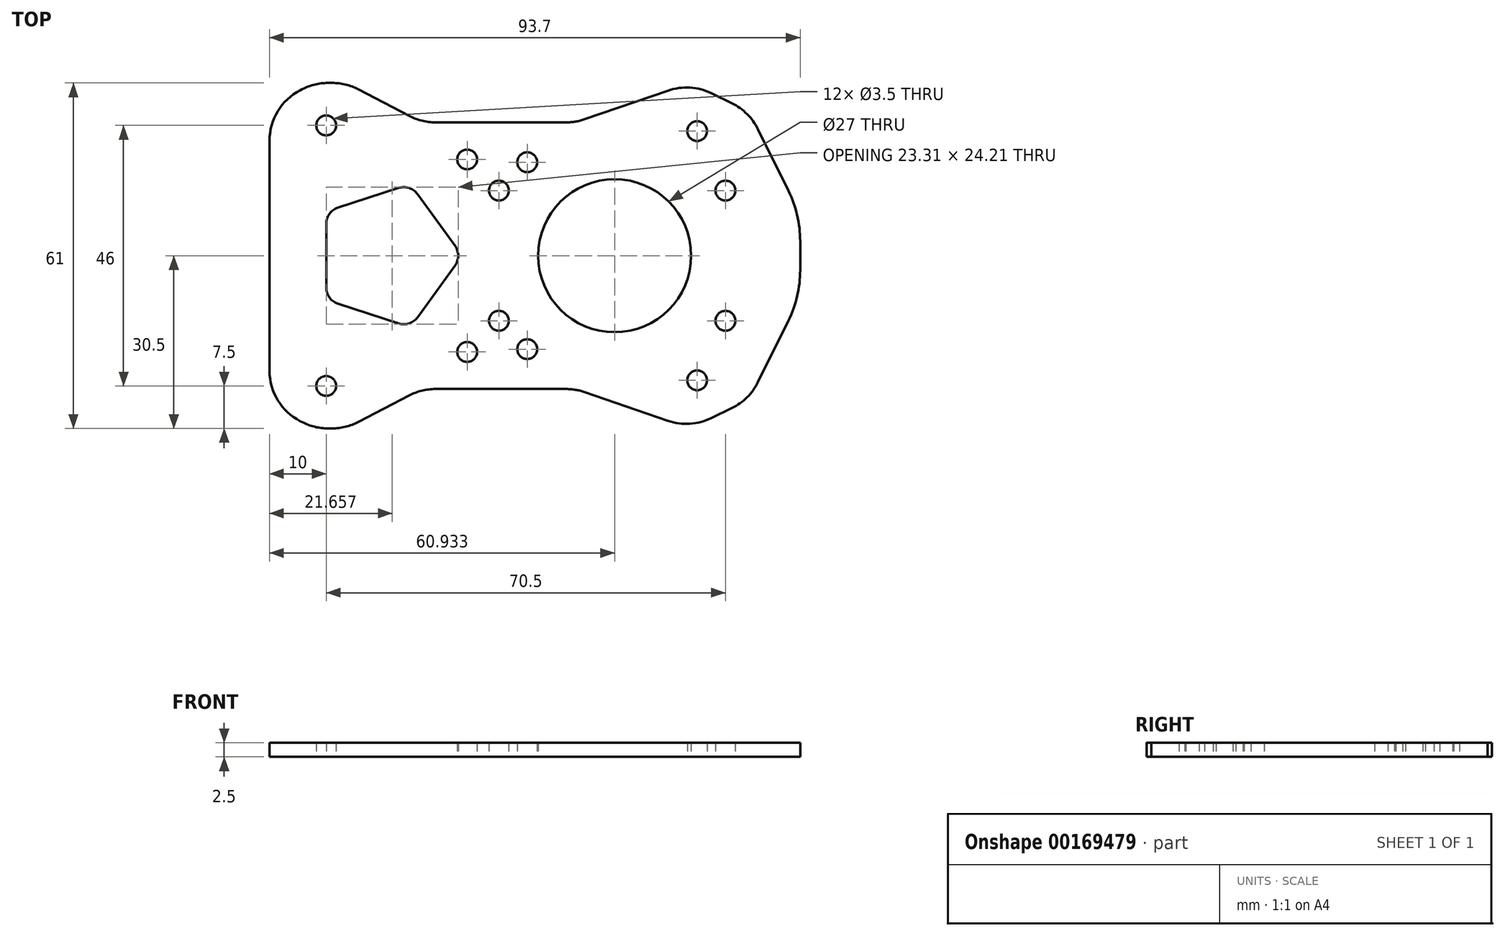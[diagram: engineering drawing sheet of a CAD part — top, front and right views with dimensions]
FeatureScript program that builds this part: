
annotation { "Feature Type Name" : "Feature", "Feature Type Description" : "" }
export const myFeature = defineFeature(function(context is Context, id is Id, definition is map)
    precondition{}
    {
        {
            var Q0;
            Q0=qCreatedBy(makeId("Top.planeOp"),FACE);
            var sketch = newSketch(context, id + "F0", { "sketchPlane" : qUnion([Q0])});
            skLineSegment(sketch, "E0.bottom", {"start": v(0, 0) * mm, "end": v(20, 0) * mm});
            skLineSegment(sketch, "E0.top", {"start": v(0, 80) * mm, "end": v(20, 80) * mm});
            skLineSegment(sketch, "E0.left", {"start": v(0, 0) * mm, "end": v(0, 80) * mm});
            skLineSegment(sketch, "E0.right", {"start": v(20, 0) * mm, "end": v(20, 11.5) * mm});
            skLineSegment(sketch, "E1.bottom", {"start": v(20, 11.5) * mm, "end": v(50, 11.5) * mm});
            skLineSegment(sketch, "E1.top", {"start": v(20, 68.5) * mm, "end": v(50, 68.5) * mm});
            skLineSegment(sketch, "E1.right", {"start": v(50, 11.5) * mm, "end": v(50, 68.5) * mm});
            skPoint(sketch, "E2", {"position": v(20, 40) * mm});
            skLineSegment(sketch, "E3.trimOffspring", {"start": v(20, 68.5) * mm, "end": v(20, 80) * mm});
            skLineSegment(sketch, "E4", {"start": v(10, 0) * mm, "end": v(0, 10) * mm});
            skLineSegment(sketch, "E5", {"start": v(0, 70) * mm, "end": v(10, 80) * mm});
            skLineSegment(sketch, "E6", {"start": v(0, 40) * mm, "end": v(50, 40) * mm, "construction": true});
            skLineSegment(sketch, "E7", {"start": v(0, 57) * mm, "end": v(50, 57) * mm, "construction": true});
            skLineSegment(sketch, "E8", {"start": v(0, 23) * mm, "end": v(50, 23) * mm, "construction": true});
            skLineSegment(sketch, "E9", {"start": v(14.5, 80) * mm, "end": v(14.5, 0) * mm, "construction": true});
            skCircle(sketch, "E10", {"center": v(14.5, 69.5) * mm, "radius": 2 * mm});
            skCircle(sketch, "E11", {"center": v(14.5, 75.5) * mm, "radius": 1.5 * mm});
            skCircle(sketch, "E12", {"center": v(14.5, 63) * mm, "radius": 1.75 * mm});
            skCircle(sketch, "E13.MirrorC", {"center": v(14.5, 17) * mm, "radius": 1.75 * mm});
            skCircle(sketch, "E14.MirrorC", {"center": v(14.5, 4.5) * mm, "radius": 1.5 * mm});
            skCircle(sketch, "E15.MirrorC", {"center": v(14.5, 10.5) * mm, "radius": 2 * mm});
            skLineSegment(sketch, "E16.0", {"start": v(0, 20.5) * mm, "end": v(50, 20.5) * mm});
            skLineSegment(sketch, "E17.0", {"start": v(0, 25.5) * mm, "end": v(50, 25.5) * mm});
            skLineSegment(sketch, "E18.MirrorCS", {"start": v(0, 54.5) * mm, "end": v(50, 54.5) * mm});
            skLineSegment(sketch, "E19.MirrorCS", {"start": v(0, 59.5) * mm, "end": v(50, 59.5) * mm});
            skSolve(sketch);
        }
        {
            var Q0;
            Q0=qCreatedBy(makeId("Top.planeOp"),FACE);
            var sketch = newSketch(context, id + "F1", { "sketchPlane" : qUnion([Q0])});
            skLineSegment(sketch, "E20", {"start": v(4.5, 70.5) * mm, "end": v(18, 70.5) * mm, "construction": true});
            skLineSegment(sketch, "E21", {"start": v(18, 70.5) * mm, "end": v(26.93, 67) * mm, "construction": true});
            skLineSegment(sketch, "E22", {"start": v(26.93, 67) * mm, "end": v(95, 67) * mm, "construction": true});
            skLineSegment(sketch, "E23", {"start": v(95, 67) * mm, "end": v(95, 40) * mm, "construction": true});
            skLineSegment(sketch, "E24", {"start": v(95, 40) * mm, "end": v(4.5, 40) * mm, "construction": true});
            skLineSegment(sketch, "E25", {"start": v(4.5, 40) * mm, "end": v(4.5, 70.5) * mm, "construction": true});
            skLineSegment(sketch, "E26.MirrorCS", {"start": v(95, 13) * mm, "end": v(95, 40) * mm, "construction": true});
            skLineSegment(sketch, "E27.MirrorCS", {"start": v(26.93, 13) * mm, "end": v(95, 13) * mm, "construction": true});
            skLineSegment(sketch, "E28.MirrorCS", {"start": v(18, 9.5) * mm, "end": v(26.93, 13) * mm, "construction": true});
            skLineSegment(sketch, "E29.MirrorCS", {"start": v(4.5, 9.5) * mm, "end": v(18, 9.5) * mm, "construction": true});
            skLineSegment(sketch, "E30.MirrorCS", {"start": v(4.5, 40) * mm, "end": v(4.5, 9.5) * mm, "construction": true});
            skCircle(sketch, "E31", {"center": v(80, 62) * mm, "radius": 1.75 * mm});
            skCircle(sketch, "E32", {"center": v(80, 18) * mm, "radius": 1.75 * mm});
            skCircle(sketch, "E33", {"center": v(85, 51.5) * mm, "radius": 1.75 * mm});
            skCircle(sketch, "E34", {"center": v(85, 28.5) * mm, "radius": 1.75 * mm});
            skLineSegment(sketch, "E35", {"start": v(32.12, 40) * mm, "end": v(170.35, 40) * mm, "construction": true});
            skCircle(sketch, "E36", {"center": v(50, 23.5) * mm, "radius": 1.75 * mm});
            skCircle(sketch, "E37", {"center": v(50, 56.5) * mm, "radius": 1.75 * mm});
            skCircle(sketch, "E38", {"center": v(45, 51.5) * mm, "radius": 1.75 * mm});
            skCircle(sketch, "E39", {"center": v(45, 28.5) * mm, "radius": 1.75 * mm});
            skCircle(sketch, "E40", {"center": v(65.43, 40) * mm, "radius": 13.5 * mm});
            skCircle(sketch, "E41.0", {"center": v(14.5, 63) * mm, "radius": 1.75 * mm});
            skCircle(sketch, "E42.0", {"center": v(14.5, 17) * mm, "radius": 1.75 * mm});
            skCircle(sketch, "E43", {"center": v(39.4, 57) * mm, "radius": 1.75 * mm});
            skCircle(sketch, "E44.MirrorC", {"center": v(39.4, 23) * mm, "radius": 1.75 * mm});
            skLineSegment(sketch, "E45", {"start": v(9.9, 69.2) * mm, "end": v(10.24, 69.38) * mm});
            skLineSegment(sketch, "E46", {"start": v(14.84, 70.5) * mm, "end": v(15.55, 70.5) * mm});
            skLineSegment(sketch, "E47", {"start": v(20.18, 69.37) * mm, "end": v(29.16, 64.68) * mm});
            skLineSegment(sketch, "E48", {"start": v(33.8, 63.54) * mm, "end": v(56.89, 63.54) * mm});
            skLineSegment(sketch, "E49", {"start": v(60.14, 64.09) * mm, "end": v(74.87, 69.15) * mm});
            skLineSegment(sketch, "E50", {"start": v(82.52, 68.68) * mm, "end": v(86.17, 66.9) * mm});
            skLineSegment(sketch, "E51", {"start": v(90.74, 62.34) * mm, "end": v(96.12, 51.45) * mm});
            skLineSegment(sketch, "E52", {"start": v(98.2, 42.58) * mm, "end": v(98.2, 40) * mm});
            skLineSegment(sketch, "E53", {"start": v(4.5, 60.32) * mm, "end": v(4.5, 40) * mm});
            skPoint(sketch, "E54.visualSharp", {"position": v(4.5, 66.4) * mm});
            skArc(sketch, "E54.filletArc", {"start": v(9.9, 69.2) * mm, "mid": v(5.96, 65.52) * mm, "end": v(4.5, 60.32) * mm});
            skPoint(sketch, "E55.visualSharp", {"position": v(12.4, 70.5) * mm});
            skArc(sketch, "E55.filletArc", {"start": v(14.84, 70.5) * mm, "mid": v(12.47, 70.22) * mm, "end": v(10.24, 69.38) * mm});
            skPoint(sketch, "E56.visualSharp", {"position": v(18, 70.5) * mm});
            skArc(sketch, "E56.filletArc", {"start": v(20.18, 69.37) * mm, "mid": v(17.94, 70.21) * mm, "end": v(15.55, 70.5) * mm});
            skPoint(sketch, "E57.visualSharp", {"position": v(31.34, 63.54) * mm});
            skArc(sketch, "E57.filletArc", {"start": v(29.16, 64.68) * mm, "mid": v(31.4, 63.83) * mm, "end": v(33.8, 63.54) * mm});
            skPoint(sketch, "E58.visualSharp", {"position": v(58.56, 63.54) * mm});
            skArc(sketch, "E58.filletArc", {"start": v(56.89, 63.54) * mm, "mid": v(58.53, 63.68) * mm, "end": v(60.14, 64.09) * mm});
            skPoint(sketch, "E59.visualSharp", {"position": v(78.8, 70.5) * mm});
            skArc(sketch, "E59.filletArc", {"start": v(82.52, 68.68) * mm, "mid": v(78.74, 69.68) * mm, "end": v(74.87, 69.15) * mm});
            skPoint(sketch, "E60.visualSharp", {"position": v(89.23, 65.4) * mm});
            skArc(sketch, "E60.filletArc", {"start": v(90.74, 62.34) * mm, "mid": v(88.83, 65) * mm, "end": v(86.17, 66.9) * mm});
            skPoint(sketch, "E61.visualSharp", {"position": v(98.2, 47.26) * mm});
            skArc(sketch, "E61.filletArc", {"start": v(98.2, 42.58) * mm, "mid": v(97.67, 47.14) * mm, "end": v(96.12, 51.45) * mm});
            skLineSegment(sketch, "E62.MirrorCS", {"start": v(4.5, 19.68) * mm, "end": v(4.5, 40) * mm});
            skArc(sketch, "E63.MirrorCS", {"start": v(9.9, 10.8) * mm, "mid": v(5.96, 14.48) * mm, "end": v(4.5, 19.68) * mm});
            skLineSegment(sketch, "E64.MirrorCS", {"start": v(9.9, 10.8) * mm, "end": v(10.24, 10.62) * mm});
            skLineSegment(sketch, "E65.MirrorCS", {"start": v(14.84, 9.5) * mm, "end": v(15.55, 9.5) * mm});
            skArc(sketch, "E66.MirrorCS", {"start": v(14.84, 9.5) * mm, "mid": v(12.47, 9.78) * mm, "end": v(10.24, 10.62) * mm});
            skArc(sketch, "E67.MirrorCS", {"start": v(20.18, 10.63) * mm, "mid": v(17.94, 9.79) * mm, "end": v(15.55, 9.5) * mm});
            skLineSegment(sketch, "E68.MirrorCS", {"start": v(20.18, 10.63) * mm, "end": v(29.16, 15.32) * mm});
            skArc(sketch, "E69.MirrorCS", {"start": v(29.16, 15.32) * mm, "mid": v(31.4, 16.17) * mm, "end": v(33.8, 16.46) * mm});
            skLineSegment(sketch, "E70.MirrorCS", {"start": v(33.8, 16.46) * mm, "end": v(56.89, 16.46) * mm});
            skArc(sketch, "E71.MirrorCS", {"start": v(56.89, 16.46) * mm, "mid": v(58.53, 16.32) * mm, "end": v(60.14, 15.91) * mm});
            skLineSegment(sketch, "E72.MirrorCS", {"start": v(60.14, 15.91) * mm, "end": v(74.87, 10.85) * mm});
            skArc(sketch, "E73.MirrorCS", {"start": v(82.52, 11.32) * mm, "mid": v(78.74, 10.32) * mm, "end": v(74.87, 10.85) * mm});
            skLineSegment(sketch, "E74.MirrorCS", {"start": v(82.52, 11.32) * mm, "end": v(86.17, 13.1) * mm});
            skArc(sketch, "E75.MirrorCS", {"start": v(90.74, 17.66) * mm, "mid": v(88.83, 15) * mm, "end": v(86.17, 13.1) * mm});
            skLineSegment(sketch, "E76.MirrorCS", {"start": v(98.2, 37.42) * mm, "end": v(98.2, 40) * mm});
            skLineSegment(sketch, "E77.MirrorCS", {"start": v(90.74, 17.66) * mm, "end": v(96.12, 28.55) * mm});
            skArc(sketch, "E78.MirrorCS", {"start": v(98.2, 37.42) * mm, "mid": v(97.67, 32.86) * mm, "end": v(96.12, 28.55) * mm});
            skCircle(sketch, "E79.cCircle", {"center": v(25.24, 40) * mm, "radius": 10.74 * mm, "construction": true});
            skLineSegment(sketch, "E79.0", {"start": v(30.63, 50.87) * mm, "end": v(37.24, 41.76) * mm});
            skLineSegment(sketch, "E79.1", {"start": v(37.24, 38.24) * mm, "end": v(30.63, 29.13) * mm});
            skLineSegment(sketch, "E79.2", {"start": v(27.27, 28.04) * mm, "end": v(16.57, 31.52) * mm});
            skLineSegment(sketch, "E79.3", {"start": v(14.5, 34.37) * mm, "end": v(14.5, 45.63) * mm});
            skLineSegment(sketch, "E79.4", {"start": v(16.57, 48.48) * mm, "end": v(27.27, 51.96) * mm});
            skPoint(sketch, "E79.0.midPoint", {"position": v(33.93, 46.31) * mm});
            skPoint(sketch, "E80.visualSharp", {"position": v(29.35, 52.63) * mm});
            skArc(sketch, "E80.filletArc", {"start": v(30.63, 50.87) * mm, "mid": v(29.13, 51.96) * mm, "end": v(27.27, 51.96) * mm});
            skPoint(sketch, "E81.visualSharp", {"position": v(38.52, 40) * mm});
            skArc(sketch, "E81.filletArc", {"start": v(37.24, 38.24) * mm, "mid": v(37.81, 40) * mm, "end": v(37.24, 41.76) * mm});
            skPoint(sketch, "E82.visualSharp", {"position": v(29.35, 27.37) * mm});
            skArc(sketch, "E82.filletArc", {"start": v(27.27, 28.04) * mm, "mid": v(29.13, 28.04) * mm, "end": v(30.63, 29.13) * mm});
            skPoint(sketch, "E83.visualSharp", {"position": v(14.5, 32.2) * mm});
            skArc(sketch, "E83.filletArc", {"start": v(14.5, 34.37) * mm, "mid": v(15.07, 32.61) * mm, "end": v(16.57, 31.52) * mm});
            skPoint(sketch, "E84.visualSharp", {"position": v(14.5, 47.8) * mm});
            skArc(sketch, "E84.filletArc", {"start": v(16.57, 48.48) * mm, "mid": v(15.07, 47.39) * mm, "end": v(14.5, 45.63) * mm});
            skSolve(sketch);
        }
        {
            var Q0;
            Q0=makeQuery(id+"F1.imprint","IMPRINT",FACE,{"disambiguationData":[TD([[makeQuery(id+"F1.imprint","IMPRINT",EDGE,{"derivedFrom":sQuery(id+"F1.wireOp",EDGE,"E20")}),-1.0]])]});
            var Q1;
            Q1=makeQuery(id+"F1.imprint","IMPRINT",FACE,{"disambiguationData":[TD([[makeQuery(id+"F1.imprint","IMPRINT",EDGE,{"derivedFrom":sQuery(id+"F1.wireOp",EDGE,"E31")}),-1.0]])]});
            extrude(context, id + "F2", {"entities" : qUnion([Q0, Q1]), "depth" : 2.5 * mm});
        }
    });
